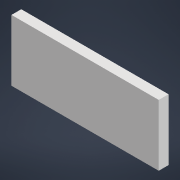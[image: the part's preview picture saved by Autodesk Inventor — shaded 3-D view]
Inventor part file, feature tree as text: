
AUTODESK INVENTOR PART (.ipt)
format: ipt  version: 2022 (Build 260153070, 153G)  size: 83,456 bytes
history: native  units: mm
features: other x1, extrude x1, sketch x1
ambient origin geometry x8: Origin, YZ Plane, XZ Plane, XY Plane, X Axis, Y Axis, Z Axis, Center Point
bodies: Body1 (feature_tree)
feature tree (3):
  other  "Твердое тело1"
  extrude  "Выдавливание1"  Depth=60.0mm
  sketch  "Эскиз1"
